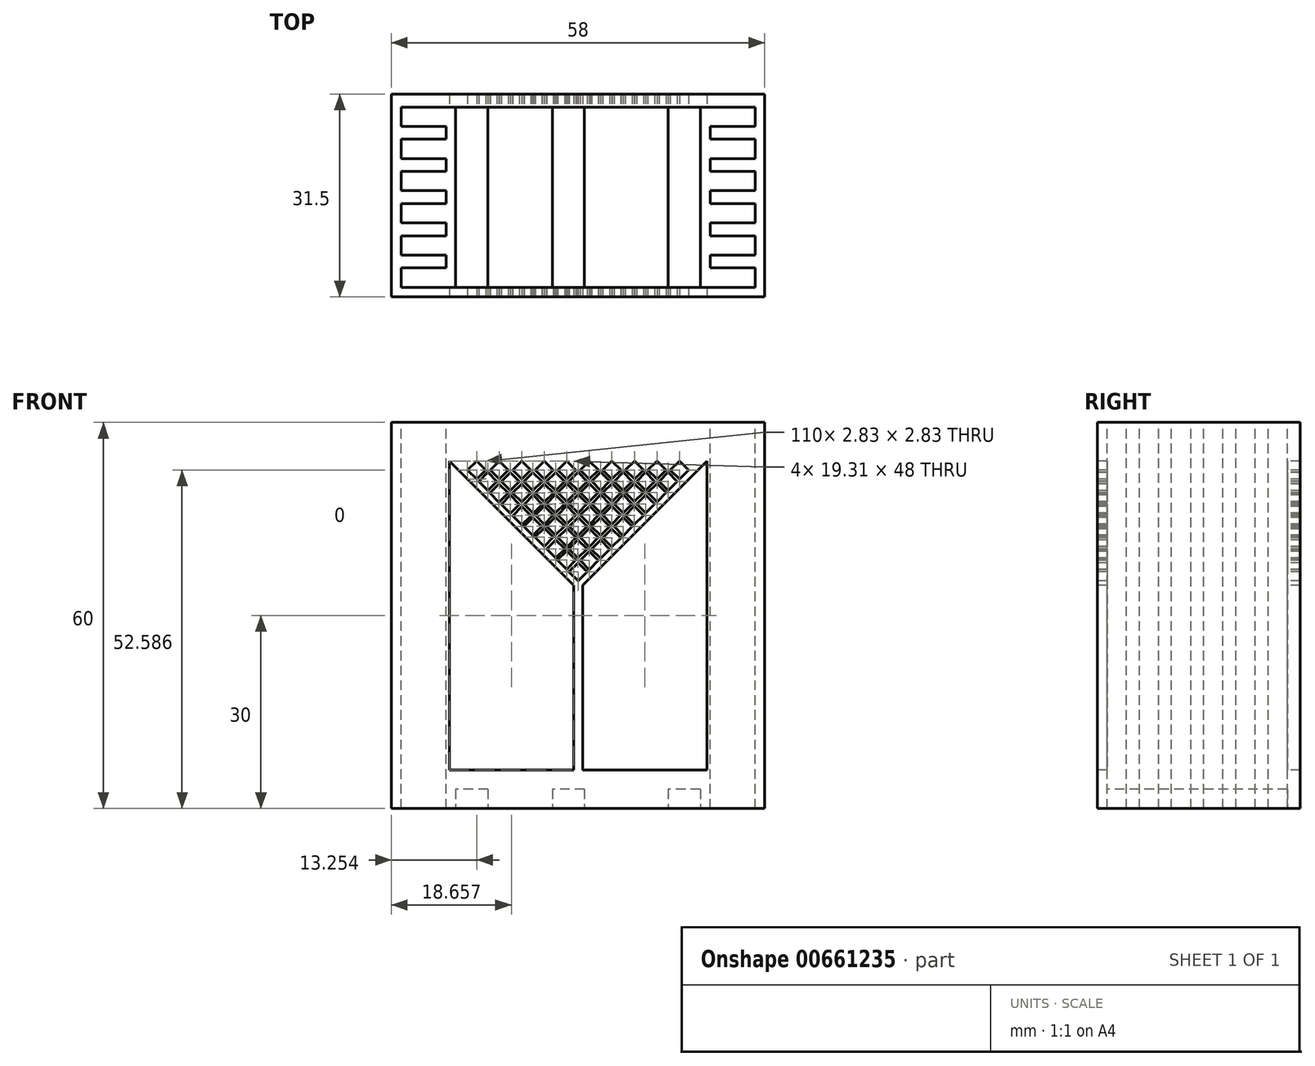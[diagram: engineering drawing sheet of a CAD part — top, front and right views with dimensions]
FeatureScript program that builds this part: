
annotation { "Feature Type Name" : "Feature", "Feature Type Description" : "" }
export const myFeature = defineFeature(function(context is Context, id is Id, definition is map)
    precondition{}
    {
        {
            var Q0;
            Q0=qCreatedBy(makeId("Top.planeOp"),FACE);
            var sketch = newSketch(context, id + "F0", { "sketchPlane" : qUnion([Q0])});
            skLineSegment(sketch, "E0.bottom", {"start": v(-21.86, 4.5) * mm, "end": v(36.14, 4.5) * mm});
            skLineSegment(sketch, "E0.left", {"start": v(-21.86, 4.5) * mm, "end": v(-21.86, -27) * mm});
            skLineSegment(sketch, "E0.right", {"start": v(36.14, 4.5) * mm, "end": v(36.14, -27) * mm});
            skLineSegment(sketch, "E1.bottom", {"start": v(-20.36, 3) * mm, "end": v(34.64, 3) * mm});
            skLineSegment(sketch, "E1.left", {"start": v(-20.36, 3) * mm, "end": v(-20.36, 0) * mm});
            skLineSegment(sketch, "E1.right", {"start": v(34.64, 3) * mm, "end": v(34.64, 0) * mm});
            skLineSegment(sketch, "E2", {"start": v(-20.36, 0) * mm, "end": v(-13.36, 0) * mm});
            skLineSegment(sketch, "E3", {"start": v(-13.36, 0) * mm, "end": v(-13.36, -2) * mm});
            skLineSegment(sketch, "E4", {"start": v(-13.36, -2) * mm, "end": v(-20.36, -2) * mm});
            skLineSegment(sketch, "E5", {"start": v(-20.36, -2) * mm, "end": v(-20.36, -5) * mm});
            skLineSegment(sketch, "E6.0.1.0", {"start": v(-20.36, -5) * mm, "end": v(-13.36, -5) * mm});
            skLineSegment(sketch, "E6.0.1.1", {"start": v(-13.36, -5) * mm, "end": v(-13.36, -7) * mm});
            skLineSegment(sketch, "E6.0.1.2", {"start": v(-20.36, -7) * mm, "end": v(-20.36, -10) * mm});
            skLineSegment(sketch, "E6.0.1.3", {"start": v(-13.36, -7) * mm, "end": v(-20.36, -7) * mm});
            skLineSegment(sketch, "E6.0.2.0", {"start": v(-20.36, -10) * mm, "end": v(-13.36, -10) * mm});
            skLineSegment(sketch, "E6.0.2.1", {"start": v(-13.36, -10) * mm, "end": v(-13.36, -12) * mm});
            skLineSegment(sketch, "E6.0.2.2", {"start": v(-20.36, -12) * mm, "end": v(-20.36, -15) * mm});
            skLineSegment(sketch, "E6.0.2.3", {"start": v(-13.36, -12) * mm, "end": v(-20.36, -12) * mm});
            skLineSegment(sketch, "E6.0.3.0", {"start": v(-20.36, -15) * mm, "end": v(-13.36, -15) * mm});
            skLineSegment(sketch, "E6.0.3.1", {"start": v(-13.36, -15) * mm, "end": v(-13.36, -17) * mm});
            skLineSegment(sketch, "E6.0.3.2", {"start": v(-20.36, -17) * mm, "end": v(-20.36, -20) * mm});
            skLineSegment(sketch, "E6.0.3.3", {"start": v(-13.36, -17) * mm, "end": v(-20.36, -17) * mm});
            skLineSegment(sketch, "E6.0.4.0", {"start": v(-20.36, -20) * mm, "end": v(-13.36, -20) * mm});
            skLineSegment(sketch, "E6.0.4.1", {"start": v(-13.36, -20) * mm, "end": v(-13.36, -22) * mm});
            skLineSegment(sketch, "E6.0.4.2", {"start": v(-20.36, -22) * mm, "end": v(-20.36, -25) * mm});
            skLineSegment(sketch, "E6.0.4.3", {"start": v(-13.36, -22) * mm, "end": v(-20.36, -22) * mm});
            skLineSegment(sketch, "E6.direction1", {"start": v(-20.36, -5) * mm, "end": v(4.64, -5) * mm, "construction": true});
            skLineSegment(sketch, "E6.direction2", {"start": v(-20.36, -5) * mm, "end": v(-20.36, -10) * mm, "construction": true});
            skLineSegment(sketch, "E7.0.1.2", {"start": v(34.64, -25) * mm, "end": v(34.64, -22) * mm});
            skLineSegment(sketch, "E7.0.2.0", {"start": v(34.64, -22) * mm, "end": v(27.64, -22) * mm});
            skLineSegment(sketch, "E7.0.2.1", {"start": v(27.64, -22) * mm, "end": v(27.64, -20) * mm});
            skLineSegment(sketch, "E7.0.2.2", {"start": v(34.64, -20) * mm, "end": v(34.64, -17) * mm});
            skLineSegment(sketch, "E7.0.2.3", {"start": v(27.64, -20) * mm, "end": v(34.64, -20) * mm});
            skLineSegment(sketch, "E7.0.3.0", {"start": v(34.64, -17) * mm, "end": v(27.64, -17) * mm});
            skLineSegment(sketch, "E7.0.3.1", {"start": v(27.64, -17) * mm, "end": v(27.64, -15) * mm});
            skLineSegment(sketch, "E7.0.3.2", {"start": v(34.64, -15) * mm, "end": v(34.64, -12) * mm});
            skLineSegment(sketch, "E7.0.3.3", {"start": v(27.64, -15) * mm, "end": v(34.64, -15) * mm});
            skLineSegment(sketch, "E7.0.4.0", {"start": v(34.64, -12) * mm, "end": v(27.64, -12) * mm});
            skLineSegment(sketch, "E7.0.4.1", {"start": v(27.64, -12) * mm, "end": v(27.64, -10) * mm});
            skLineSegment(sketch, "E7.0.4.2", {"start": v(34.64, -10) * mm, "end": v(34.64, -7) * mm});
            skLineSegment(sketch, "E7.0.4.3", {"start": v(27.64, -10) * mm, "end": v(34.64, -10) * mm});
            skLineSegment(sketch, "E7.0.5.0", {"start": v(34.64, -7) * mm, "end": v(27.64, -7) * mm});
            skLineSegment(sketch, "E7.0.5.1", {"start": v(27.64, -7) * mm, "end": v(27.64, -5) * mm});
            skLineSegment(sketch, "E7.0.5.2", {"start": v(34.64, -5) * mm, "end": v(34.64, -2) * mm});
            skLineSegment(sketch, "E7.0.5.3", {"start": v(27.64, -5) * mm, "end": v(34.64, -5) * mm});
            skLineSegment(sketch, "E7.0.6.0", {"start": v(34.64, -2) * mm, "end": v(27.64, -2) * mm});
            skLineSegment(sketch, "E7.0.6.1", {"start": v(27.64, -2) * mm, "end": v(27.64, 0) * mm});
            skLineSegment(sketch, "E7.0.6.2", {"start": v(34.64, 0) * mm, "end": v(34.64, 3) * mm});
            skLineSegment(sketch, "E7.0.6.3", {"start": v(27.64, 0) * mm, "end": v(34.64, 0) * mm});
            skLineSegment(sketch, "E7.direction2", {"start": v(34.64, -27) * mm, "end": v(34.64, -22) * mm, "construction": true});
            skLineSegment(sketch, "E8", {"start": v(36.14, -27) * mm, "end": v(-21.86, -27) * mm});
            skLineSegment(sketch, "E9", {"start": v(34.64, -25) * mm, "end": v(-20.36, -25) * mm});
            skSolve(sketch);
        }
        {
            var Q0;
            Q0=makeQuery(id+"F0.imprint","IMPRINT",FACE,{"disambiguationData":[TD([[makeQuery(id+"F0.imprint","IMPRINT",EDGE,{"derivedFrom":sQuery(id+"F0.wireOp",EDGE,"E0.bottom")}),-1.0]])]});
            extrude(context, id + "F1", {"entities" : qUnion([Q0]), "depth" : 60 * mm, "offsetDistance" : 25 * mm});
        }
        {
            var Q0;
            Q0=makeQuery(id+"F1.opExtrude","SWEPT_FACE",FACE,{"disambiguationData":[OSD([sQuery(id+"F0.wireOp",EDGE,"E0.bottom")])]});
            var sketch = newSketch(context, id + "F2", { "sketchPlane" : qUnion([Q0])});
            skLineSegment(sketch, "E10.bottom", {"start": v(-27.14, 6) * mm, "end": v(12.86, 6) * mm});
            skLineSegment(sketch, "E10.top", {"start": v(-27.14, 54) * mm, "end": v(12.86, 54) * mm});
            skLineSegment(sketch, "E10.left", {"start": v(-27.14, 6) * mm, "end": v(-27.14, 54) * mm});
            skLineSegment(sketch, "E10.right", {"start": v(12.86, 6) * mm, "end": v(12.86, 54) * mm});
            skLineSegment(sketch, "E11", {"start": v(12.86, 6) * mm, "end": v(-6.45, 25.3) * mm});
            skLineSegment(sketch, "E12", {"start": v(-6.45, 25.3) * mm, "end": v(-6.45, 54) * mm});
            skLineSegment(sketch, "E13", {"start": v(-6.45, 54) * mm, "end": v(-7.84, 54) * mm});
            skLineSegment(sketch, "E14", {"start": v(-7.84, 54) * mm, "end": v(-7.84, 25.3) * mm});
            skLineSegment(sketch, "E15", {"start": v(-7.84, 25.3) * mm, "end": v(-27.14, 6) * mm});
            skLineSegment(sketch, "E16", {"start": v(8.6, 6) * mm, "end": v(10.02, 7.41) * mm});
            skLineSegment(sketch, "E17", {"start": v(10.02, 7.41) * mm, "end": v(8.6, 8.83) * mm});
            skLineSegment(sketch, "E18", {"start": v(8.6, 8.83) * mm, "end": v(7.2, 7.41) * mm});
            skLineSegment(sketch, "E19", {"start": v(7.2, 7.41) * mm, "end": v(8.6, 6) * mm});
            skLineSegment(sketch, "E20.1.0.0", {"start": v(6.52, 7.41) * mm, "end": v(5.1, 8.83) * mm});
            skLineSegment(sketch, "E20.1.0.1", {"start": v(5.1, 8.83) * mm, "end": v(3.7, 7.41) * mm});
            skLineSegment(sketch, "E20.1.0.2", {"start": v(3.7, 7.41) * mm, "end": v(5.1, 6) * mm});
            skLineSegment(sketch, "E20.1.0.3", {"start": v(5.1, 6) * mm, "end": v(6.52, 7.41) * mm});
            skLineSegment(sketch, "E20.2.0.0", {"start": v(3.02, 7.41) * mm, "end": v(1.6, 8.83) * mm});
            skLineSegment(sketch, "E20.2.0.1", {"start": v(1.6, 8.83) * mm, "end": v(0.2, 7.41) * mm});
            skLineSegment(sketch, "E20.2.0.2", {"start": v(0.2, 7.41) * mm, "end": v(1.6, 6) * mm});
            skLineSegment(sketch, "E20.2.0.3", {"start": v(1.6, 6) * mm, "end": v(3.02, 7.41) * mm});
            skLineSegment(sketch, "E20.3.0.0", {"start": v(-0.48, 7.41) * mm, "end": v(-1.9, 8.83) * mm});
            skLineSegment(sketch, "E20.3.0.1", {"start": v(-1.9, 8.83) * mm, "end": v(-3.3, 7.41) * mm});
            skLineSegment(sketch, "E20.3.0.2", {"start": v(-3.3, 7.41) * mm, "end": v(-1.9, 6) * mm});
            skLineSegment(sketch, "E20.3.0.3", {"start": v(-1.9, 6) * mm, "end": v(-0.48, 7.41) * mm});
            skLineSegment(sketch, "E20.4.0.0", {"start": v(-3.98, 7.41) * mm, "end": v(-5.4, 8.83) * mm});
            skLineSegment(sketch, "E20.4.0.1", {"start": v(-5.4, 8.83) * mm, "end": v(-6.8, 7.41) * mm});
            skLineSegment(sketch, "E20.4.0.2", {"start": v(-6.8, 7.41) * mm, "end": v(-5.4, 6) * mm});
            skLineSegment(sketch, "E20.4.0.3", {"start": v(-5.4, 6) * mm, "end": v(-3.98, 7.41) * mm});
            skLineSegment(sketch, "E20.5.0.0", {"start": v(-7.48, 7.41) * mm, "end": v(-8.9, 8.83) * mm});
            skLineSegment(sketch, "E20.5.0.1", {"start": v(-8.9, 8.83) * mm, "end": v(-10.3, 7.41) * mm});
            skLineSegment(sketch, "E20.5.0.2", {"start": v(-10.3, 7.41) * mm, "end": v(-8.9, 6) * mm});
            skLineSegment(sketch, "E20.5.0.3", {"start": v(-8.9, 6) * mm, "end": v(-7.48, 7.41) * mm});
            skLineSegment(sketch, "E20.6.0.0", {"start": v(-10.98, 7.41) * mm, "end": v(-12.4, 8.83) * mm});
            skLineSegment(sketch, "E20.6.0.1", {"start": v(-12.4, 8.83) * mm, "end": v(-13.8, 7.41) * mm});
            skLineSegment(sketch, "E20.6.0.2", {"start": v(-13.8, 7.41) * mm, "end": v(-12.4, 6) * mm});
            skLineSegment(sketch, "E20.6.0.3", {"start": v(-12.4, 6) * mm, "end": v(-10.98, 7.41) * mm});
            skLineSegment(sketch, "E20.direction1", {"start": v(10.02, 7.41) * mm, "end": v(6.52, 7.41) * mm, "construction": true});
            skLineSegment(sketch, "E21.0.7.0", {"start": v(-14.48, 7.41) * mm, "end": v(-15.9, 8.83) * mm});
            skLineSegment(sketch, "E21.3.7.0", {"start": v(-15.9, 8.83) * mm, "end": v(-17.3, 7.41) * mm});
            skLineSegment(sketch, "E21.6.7.0", {"start": v(-17.3, 7.41) * mm, "end": v(-15.9, 6) * mm});
            skLineSegment(sketch, "E21.9.7.0", {"start": v(-15.9, 6) * mm, "end": v(-14.48, 7.41) * mm});
            skLineSegment(sketch, "E21.0.8.0", {"start": v(-17.98, 7.41) * mm, "end": v(-19.4, 8.83) * mm});
            skLineSegment(sketch, "E21.3.8.0", {"start": v(-19.4, 8.83) * mm, "end": v(-20.8, 7.41) * mm});
            skLineSegment(sketch, "E21.6.8.0", {"start": v(-20.8, 7.41) * mm, "end": v(-19.4, 6) * mm});
            skLineSegment(sketch, "E21.9.8.0", {"start": v(-19.4, 6) * mm, "end": v(-17.98, 7.41) * mm});
            skLineSegment(sketch, "E22.0.9.0", {"start": v(-21.48, 7.41) * mm, "end": v(-22.9, 8.83) * mm});
            skLineSegment(sketch, "E22.3.9.0", {"start": v(-22.9, 8.83) * mm, "end": v(-24.3, 7.41) * mm});
            skLineSegment(sketch, "E22.6.9.0", {"start": v(-24.3, 7.41) * mm, "end": v(-22.9, 6) * mm});
            skLineSegment(sketch, "E22.9.9.0", {"start": v(-22.9, 6) * mm, "end": v(-21.48, 7.41) * mm});
            skLineSegment(sketch, "E23.direction1", {"start": v(6.87, 7.77) * mm, "end": v(3.37, 7.77) * mm, "construction": true});
            skLineSegment(sketch, "E24.1.0.0", {"start": v(-19.73, 9.17) * mm, "end": v(-21.14, 10.58) * mm});
            skLineSegment(sketch, "E24.1.0.1", {"start": v(-21.14, 10.58) * mm, "end": v(-22.56, 9.17) * mm});
            skLineSegment(sketch, "E24.1.0.2", {"start": v(-21.14, 7.76) * mm, "end": v(-19.73, 9.17) * mm});
            skLineSegment(sketch, "E24.1.0.3", {"start": v(-22.56, 9.17) * mm, "end": v(-21.14, 7.76) * mm});
            skLineSegment(sketch, "E24.2.0.0", {"start": v(-17.98, 10.93) * mm, "end": v(-19.4, 12.34) * mm});
            skLineSegment(sketch, "E24.2.0.1", {"start": v(-19.4, 12.34) * mm, "end": v(-20.8, 10.93) * mm});
            skLineSegment(sketch, "E24.2.0.2", {"start": v(-19.4, 9.51) * mm, "end": v(-17.98, 10.93) * mm});
            skLineSegment(sketch, "E24.2.0.3", {"start": v(-20.8, 10.93) * mm, "end": v(-19.4, 9.51) * mm});
            skLineSegment(sketch, "E24.3.0.0", {"start": v(-16.23, 12.68) * mm, "end": v(-17.64, 14.1) * mm});
            skLineSegment(sketch, "E24.3.0.1", {"start": v(-17.64, 14.1) * mm, "end": v(-19.06, 12.68) * mm});
            skLineSegment(sketch, "E24.3.0.2", {"start": v(-17.64, 11.27) * mm, "end": v(-16.23, 12.68) * mm});
            skLineSegment(sketch, "E24.3.0.3", {"start": v(-19.06, 12.68) * mm, "end": v(-17.64, 11.27) * mm});
            skLineSegment(sketch, "E24.4.0.0", {"start": v(-14.48, 14.44) * mm, "end": v(-15.9, 15.85) * mm});
            skLineSegment(sketch, "E24.4.0.1", {"start": v(-15.9, 15.85) * mm, "end": v(-17.3, 14.44) * mm});
            skLineSegment(sketch, "E24.4.0.2", {"start": v(-15.9, 13.03) * mm, "end": v(-14.48, 14.44) * mm});
            skLineSegment(sketch, "E24.4.0.3", {"start": v(-17.3, 14.44) * mm, "end": v(-15.9, 13.03) * mm});
            skLineSegment(sketch, "E24.5.0.0", {"start": v(-12.73, 16.2) * mm, "end": v(-14.14, 17.61) * mm});
            skLineSegment(sketch, "E24.5.0.1", {"start": v(-14.14, 17.61) * mm, "end": v(-15.55, 16.2) * mm});
            skLineSegment(sketch, "E24.5.0.2", {"start": v(-14.14, 14.78) * mm, "end": v(-12.73, 16.2) * mm});
            skLineSegment(sketch, "E24.5.0.3", {"start": v(-15.55, 16.2) * mm, "end": v(-14.14, 14.78) * mm});
            skLineSegment(sketch, "E24.6.0.0", {"start": v(-10.97, 17.95) * mm, "end": v(-12.39, 19.37) * mm});
            skLineSegment(sketch, "E24.6.0.1", {"start": v(-12.39, 19.37) * mm, "end": v(-13.8, 17.95) * mm});
            skLineSegment(sketch, "E24.6.0.2", {"start": v(-12.39, 16.54) * mm, "end": v(-10.97, 17.95) * mm});
            skLineSegment(sketch, "E24.6.0.3", {"start": v(-13.8, 17.95) * mm, "end": v(-12.39, 16.54) * mm});
            skLineSegment(sketch, "E24.7.0.0", {"start": v(-9.22, 19.7) * mm, "end": v(-10.64, 21.12) * mm});
            skLineSegment(sketch, "E24.7.0.1", {"start": v(-10.64, 21.12) * mm, "end": v(-12.05, 19.7) * mm});
            skLineSegment(sketch, "E24.7.0.2", {"start": v(-10.64, 18.3) * mm, "end": v(-9.22, 19.7) * mm});
            skLineSegment(sketch, "E24.7.0.3", {"start": v(-12.05, 19.7) * mm, "end": v(-10.64, 18.3) * mm});
            skLineSegment(sketch, "E24.8.0.0", {"start": v(-7.47, 21.47) * mm, "end": v(-8.89, 22.88) * mm});
            skLineSegment(sketch, "E24.8.0.1", {"start": v(-8.89, 22.88) * mm, "end": v(-10.3, 21.47) * mm});
            skLineSegment(sketch, "E24.8.0.2", {"start": v(-8.89, 20.05) * mm, "end": v(-7.47, 21.47) * mm});
            skLineSegment(sketch, "E24.8.0.3", {"start": v(-10.3, 21.47) * mm, "end": v(-8.89, 20.05) * mm});
            skLineSegment(sketch, "E24.9.0.0", {"start": v(-5.72, 23.22) * mm, "end": v(-7.14, 24.64) * mm});
            skLineSegment(sketch, "E24.9.0.1", {"start": v(-7.14, 24.64) * mm, "end": v(-8.55, 23.22) * mm});
            skLineSegment(sketch, "E24.9.0.2", {"start": v(-7.14, 21.8) * mm, "end": v(-5.72, 23.22) * mm});
            skLineSegment(sketch, "E24.9.0.3", {"start": v(-8.55, 23.22) * mm, "end": v(-7.14, 21.8) * mm});
            skLineSegment(sketch, "E24.direction1", {"start": v(-22.9, 6) * mm, "end": v(-21.14, 7.76) * mm, "construction": true});
            skLineSegment(sketch, "E25.1.0.0", {"start": v(-17.64, 7.75) * mm, "end": v(-16.23, 9.16) * mm});
            skLineSegment(sketch, "E25.1.0.1", {"start": v(-19.05, 9.16) * mm, "end": v(-17.64, 7.75) * mm});
            skLineSegment(sketch, "E25.1.0.2", {"start": v(-17.64, 10.58) * mm, "end": v(-19.05, 9.16) * mm});
            skLineSegment(sketch, "E25.1.0.3", {"start": v(-16.23, 9.16) * mm, "end": v(-17.64, 10.58) * mm});
            skLineSegment(sketch, "E25.2.0.0", {"start": v(-15.89, 9.5) * mm, "end": v(-14.47, 10.91) * mm});
            skLineSegment(sketch, "E25.2.0.1", {"start": v(-17.3, 10.91) * mm, "end": v(-15.89, 9.5) * mm});
            skLineSegment(sketch, "E25.2.0.2", {"start": v(-15.89, 12.33) * mm, "end": v(-17.3, 10.91) * mm});
            skLineSegment(sketch, "E25.2.0.3", {"start": v(-14.47, 10.91) * mm, "end": v(-15.89, 12.33) * mm});
            skLineSegment(sketch, "E25.3.0.0", {"start": v(-14.13, 11.25) * mm, "end": v(-12.72, 12.66) * mm});
            skLineSegment(sketch, "E25.3.0.1", {"start": v(-15.55, 12.66) * mm, "end": v(-14.13, 11.25) * mm});
            skLineSegment(sketch, "E25.3.0.2", {"start": v(-14.13, 14.08) * mm, "end": v(-15.55, 12.66) * mm});
            skLineSegment(sketch, "E25.3.0.3", {"start": v(-12.72, 12.66) * mm, "end": v(-14.13, 14.08) * mm});
            skLineSegment(sketch, "E25.4.0.0", {"start": v(-12.38, 13) * mm, "end": v(-10.96, 14.41) * mm});
            skLineSegment(sketch, "E25.4.0.1", {"start": v(-13.8, 14.41) * mm, "end": v(-12.38, 13) * mm});
            skLineSegment(sketch, "E25.4.0.2", {"start": v(-12.38, 15.83) * mm, "end": v(-13.8, 14.41) * mm});
            skLineSegment(sketch, "E25.4.0.3", {"start": v(-10.96, 14.41) * mm, "end": v(-12.38, 15.83) * mm});
            skLineSegment(sketch, "E25.5.0.0", {"start": v(-10.63, 14.75) * mm, "end": v(-9.21, 16.16) * mm});
            skLineSegment(sketch, "E25.5.0.1", {"start": v(-12.04, 16.16) * mm, "end": v(-10.63, 14.75) * mm});
            skLineSegment(sketch, "E25.5.0.2", {"start": v(-10.63, 17.58) * mm, "end": v(-12.04, 16.16) * mm});
            skLineSegment(sketch, "E25.5.0.3", {"start": v(-9.21, 16.16) * mm, "end": v(-10.63, 17.58) * mm});
            skLineSegment(sketch, "E25.6.0.0", {"start": v(-8.87, 16.5) * mm, "end": v(-7.46, 17.91) * mm});
            skLineSegment(sketch, "E25.6.0.1", {"start": v(-10.29, 17.91) * mm, "end": v(-8.87, 16.5) * mm});
            skLineSegment(sketch, "E25.6.0.2", {"start": v(-8.87, 19.33) * mm, "end": v(-10.29, 17.91) * mm});
            skLineSegment(sketch, "E25.6.0.3", {"start": v(-7.46, 17.91) * mm, "end": v(-8.87, 19.33) * mm});
            skLineSegment(sketch, "E25.7.0.0", {"start": v(-7.12, 18.25) * mm, "end": v(-5.7, 19.66) * mm});
            skLineSegment(sketch, "E25.7.0.1", {"start": v(-8.53, 19.66) * mm, "end": v(-7.12, 18.25) * mm});
            skLineSegment(sketch, "E25.7.0.2", {"start": v(-7.12, 21.08) * mm, "end": v(-8.53, 19.66) * mm});
            skLineSegment(sketch, "E25.7.0.3", {"start": v(-5.7, 19.66) * mm, "end": v(-7.12, 21.08) * mm});
            skLineSegment(sketch, "E25.8.0.0", {"start": v(-5.36, 20) * mm, "end": v(-3.95, 21.41) * mm});
            skLineSegment(sketch, "E25.8.0.1", {"start": v(-6.78, 21.41) * mm, "end": v(-5.36, 20) * mm});
            skLineSegment(sketch, "E25.8.0.2", {"start": v(-5.36, 22.83) * mm, "end": v(-6.78, 21.41) * mm});
            skLineSegment(sketch, "E25.8.0.3", {"start": v(-3.95, 21.41) * mm, "end": v(-5.36, 22.83) * mm});
            skLineSegment(sketch, "E25.direction1", {"start": v(-19.4, 6) * mm, "end": v(-17.64, 7.75) * mm, "construction": true});
            skLineSegment(sketch, "E26.1.0.0", {"start": v(-14.15, 7.75) * mm, "end": v(-12.74, 9.16) * mm});
            skLineSegment(sketch, "E26.1.0.1", {"start": v(-15.56, 9.16) * mm, "end": v(-14.15, 7.75) * mm});
            skLineSegment(sketch, "E26.1.0.2", {"start": v(-14.15, 10.58) * mm, "end": v(-15.56, 9.16) * mm});
            skLineSegment(sketch, "E26.1.0.3", {"start": v(-12.74, 9.16) * mm, "end": v(-14.15, 10.58) * mm});
            skLineSegment(sketch, "E26.2.0.0", {"start": v(-12.4, 9.5) * mm, "end": v(-11, 10.91) * mm});
            skLineSegment(sketch, "E26.2.0.1", {"start": v(-13.82, 10.91) * mm, "end": v(-12.4, 9.5) * mm});
            skLineSegment(sketch, "E26.2.0.2", {"start": v(-12.4, 12.33) * mm, "end": v(-13.82, 10.91) * mm});
            skLineSegment(sketch, "E26.2.0.3", {"start": v(-11, 10.91) * mm, "end": v(-12.4, 12.33) * mm});
            skLineSegment(sketch, "E26.3.0.0", {"start": v(-10.66, 11.25) * mm, "end": v(-9.25, 12.66) * mm});
            skLineSegment(sketch, "E26.3.0.1", {"start": v(-12.08, 12.66) * mm, "end": v(-10.66, 11.25) * mm});
            skLineSegment(sketch, "E26.3.0.2", {"start": v(-10.66, 14.08) * mm, "end": v(-12.08, 12.66) * mm});
            skLineSegment(sketch, "E26.3.0.3", {"start": v(-9.25, 12.66) * mm, "end": v(-10.66, 14.08) * mm});
            skLineSegment(sketch, "E26.4.0.0", {"start": v(-8.92, 13) * mm, "end": v(-7.5, 14.41) * mm});
            skLineSegment(sketch, "E26.4.0.1", {"start": v(-10.33, 14.41) * mm, "end": v(-8.92, 13) * mm});
            skLineSegment(sketch, "E26.4.0.2", {"start": v(-8.92, 15.83) * mm, "end": v(-10.33, 14.41) * mm});
            skLineSegment(sketch, "E26.4.0.3", {"start": v(-7.5, 14.41) * mm, "end": v(-8.92, 15.83) * mm});
            skLineSegment(sketch, "E26.5.0.0", {"start": v(-7.18, 14.75) * mm, "end": v(-5.76, 16.16) * mm});
            skLineSegment(sketch, "E26.5.0.1", {"start": v(-8.59, 16.16) * mm, "end": v(-7.18, 14.75) * mm});
            skLineSegment(sketch, "E26.5.0.2", {"start": v(-7.18, 17.58) * mm, "end": v(-8.59, 16.16) * mm});
            skLineSegment(sketch, "E26.5.0.3", {"start": v(-5.76, 16.16) * mm, "end": v(-7.18, 17.58) * mm});
            skLineSegment(sketch, "E26.6.0.0", {"start": v(-5.43, 16.5) * mm, "end": v(-4.02, 17.91) * mm});
            skLineSegment(sketch, "E26.6.0.1", {"start": v(-6.85, 17.91) * mm, "end": v(-5.43, 16.5) * mm});
            skLineSegment(sketch, "E26.6.0.2", {"start": v(-5.43, 19.33) * mm, "end": v(-6.85, 17.91) * mm});
            skLineSegment(sketch, "E26.6.0.3", {"start": v(-4.02, 17.91) * mm, "end": v(-5.43, 19.33) * mm});
            skLineSegment(sketch, "E26.7.0.0", {"start": v(-3.69, 18.25) * mm, "end": v(-2.27, 19.66) * mm});
            skLineSegment(sketch, "E26.7.0.1", {"start": v(-5.1, 19.66) * mm, "end": v(-3.69, 18.25) * mm});
            skLineSegment(sketch, "E26.7.0.2", {"start": v(-3.69, 21.08) * mm, "end": v(-5.1, 19.66) * mm});
            skLineSegment(sketch, "E26.7.0.3", {"start": v(-2.27, 19.66) * mm, "end": v(-3.69, 21.08) * mm});
            skLineSegment(sketch, "E26.direction1", {"start": v(-15.9, 6) * mm, "end": v(-14.15, 7.75) * mm, "construction": true});
            skLineSegment(sketch, "E27.1.0.0", {"start": v(-10.64, 7.74) * mm, "end": v(-9.23, 9.15) * mm});
            skLineSegment(sketch, "E27.1.0.1", {"start": v(-9.23, 9.15) * mm, "end": v(-10.64, 10.57) * mm});
            skLineSegment(sketch, "E27.1.0.2", {"start": v(-10.64, 10.57) * mm, "end": v(-12.05, 9.15) * mm});
            skLineSegment(sketch, "E27.1.0.3", {"start": v(-12.05, 9.15) * mm, "end": v(-10.64, 7.74) * mm});
            skLineSegment(sketch, "E27.2.0.0", {"start": v(-8.89, 9.48) * mm, "end": v(-7.47, 10.9) * mm});
            skLineSegment(sketch, "E27.2.0.1", {"start": v(-7.47, 10.9) * mm, "end": v(-8.89, 12.3) * mm});
            skLineSegment(sketch, "E27.2.0.2", {"start": v(-8.89, 12.3) * mm, "end": v(-10.3, 10.9) * mm});
            skLineSegment(sketch, "E27.2.0.3", {"start": v(-10.3, 10.9) * mm, "end": v(-8.89, 9.48) * mm});
            skLineSegment(sketch, "E27.3.0.0", {"start": v(-7.13, 11.22) * mm, "end": v(-5.72, 12.63) * mm});
            skLineSegment(sketch, "E27.3.0.1", {"start": v(-5.72, 12.63) * mm, "end": v(-7.13, 14.05) * mm});
            skLineSegment(sketch, "E27.3.0.2", {"start": v(-7.13, 14.05) * mm, "end": v(-8.55, 12.63) * mm});
            skLineSegment(sketch, "E27.3.0.3", {"start": v(-8.55, 12.63) * mm, "end": v(-7.13, 11.22) * mm});
            skLineSegment(sketch, "E27.4.0.0", {"start": v(-5.38, 12.96) * mm, "end": v(-3.96, 14.37) * mm});
            skLineSegment(sketch, "E27.4.0.1", {"start": v(-3.96, 14.37) * mm, "end": v(-5.38, 15.79) * mm});
            skLineSegment(sketch, "E27.4.0.2", {"start": v(-5.38, 15.79) * mm, "end": v(-6.8, 14.37) * mm});
            skLineSegment(sketch, "E27.4.0.3", {"start": v(-6.8, 14.37) * mm, "end": v(-5.38, 12.96) * mm});
            skLineSegment(sketch, "E27.5.0.0", {"start": v(-3.63, 14.7) * mm, "end": v(-2.21, 16.11) * mm});
            skLineSegment(sketch, "E27.5.0.1", {"start": v(-2.21, 16.11) * mm, "end": v(-3.63, 17.53) * mm});
            skLineSegment(sketch, "E27.5.0.2", {"start": v(-3.63, 17.53) * mm, "end": v(-5.04, 16.11) * mm});
            skLineSegment(sketch, "E27.5.0.3", {"start": v(-5.04, 16.11) * mm, "end": v(-3.63, 14.7) * mm});
            skLineSegment(sketch, "E27.6.0.0", {"start": v(-1.87, 16.44) * mm, "end": v(-0.46, 17.85) * mm});
            skLineSegment(sketch, "E27.6.0.1", {"start": v(-0.46, 17.85) * mm, "end": v(-1.87, 19.27) * mm});
            skLineSegment(sketch, "E27.6.0.2", {"start": v(-1.87, 19.27) * mm, "end": v(-3.29, 17.85) * mm});
            skLineSegment(sketch, "E27.6.0.3", {"start": v(-3.29, 17.85) * mm, "end": v(-1.87, 16.44) * mm});
            skLineSegment(sketch, "E27.direction1", {"start": v(-12.4, 6) * mm, "end": v(-10.64, 7.74) * mm, "construction": true});
            skLineSegment(sketch, "E28.1.0.0", {"start": v(-5.73, 9.16) * mm, "end": v(-7.14, 10.58) * mm});
            skLineSegment(sketch, "E28.1.0.1", {"start": v(-7.14, 7.75) * mm, "end": v(-5.73, 9.16) * mm});
            skLineSegment(sketch, "E28.1.0.2", {"start": v(-8.55, 9.16) * mm, "end": v(-7.14, 7.75) * mm});
            skLineSegment(sketch, "E28.1.0.3", {"start": v(-7.14, 10.58) * mm, "end": v(-8.55, 9.16) * mm});
            skLineSegment(sketch, "E28.2.0.0", {"start": v(-3.97, 10.91) * mm, "end": v(-5.39, 12.33) * mm});
            skLineSegment(sketch, "E28.2.0.1", {"start": v(-5.39, 9.5) * mm, "end": v(-3.97, 10.91) * mm});
            skLineSegment(sketch, "E28.2.0.2", {"start": v(-6.8, 10.91) * mm, "end": v(-5.39, 9.5) * mm});
            skLineSegment(sketch, "E28.2.0.3", {"start": v(-5.39, 12.33) * mm, "end": v(-6.8, 10.91) * mm});
            skLineSegment(sketch, "E28.3.0.0", {"start": v(-2.22, 12.66) * mm, "end": v(-3.63, 14.08) * mm});
            skLineSegment(sketch, "E28.3.0.1", {"start": v(-3.63, 11.25) * mm, "end": v(-2.22, 12.66) * mm});
            skLineSegment(sketch, "E28.3.0.2", {"start": v(-5.05, 12.66) * mm, "end": v(-3.63, 11.25) * mm});
            skLineSegment(sketch, "E28.3.0.3", {"start": v(-3.63, 14.08) * mm, "end": v(-5.05, 12.66) * mm});
            skLineSegment(sketch, "E28.4.0.0", {"start": v(-0.46, 14.41) * mm, "end": v(-1.88, 15.83) * mm});
            skLineSegment(sketch, "E28.4.0.1", {"start": v(-1.88, 13) * mm, "end": v(-0.46, 14.41) * mm});
            skLineSegment(sketch, "E28.4.0.2", {"start": v(-3.3, 14.41) * mm, "end": v(-1.88, 13) * mm});
            skLineSegment(sketch, "E28.4.0.3", {"start": v(-1.88, 15.83) * mm, "end": v(-3.3, 14.41) * mm});
            skLineSegment(sketch, "E28.5.0.0", {"start": v(1.29, 16.16) * mm, "end": v(-0.13, 17.58) * mm});
            skLineSegment(sketch, "E28.5.0.1", {"start": v(-0.13, 14.75) * mm, "end": v(1.29, 16.16) * mm});
            skLineSegment(sketch, "E28.5.0.2", {"start": v(-1.54, 16.16) * mm, "end": v(-0.13, 14.75) * mm});
            skLineSegment(sketch, "E28.5.0.3", {"start": v(-0.13, 17.58) * mm, "end": v(-1.54, 16.16) * mm});
            skLineSegment(sketch, "E28.direction1", {"start": v(-8.9, 6) * mm, "end": v(-7.14, 7.75) * mm, "construction": true});
            skLineSegment(sketch, "E29.1.0.0", {"start": v(-2.24, 9.18) * mm, "end": v(-3.65, 10.6) * mm});
            skLineSegment(sketch, "E29.1.0.1", {"start": v(-3.65, 7.77) * mm, "end": v(-2.24, 9.18) * mm});
            skLineSegment(sketch, "E29.1.0.2", {"start": v(-5.06, 9.18) * mm, "end": v(-3.65, 7.77) * mm});
            skLineSegment(sketch, "E29.1.0.3", {"start": v(-3.65, 10.6) * mm, "end": v(-5.06, 9.18) * mm});
            skLineSegment(sketch, "E29.2.0.0", {"start": v(-0.5, 10.95) * mm, "end": v(-1.9, 12.37) * mm});
            skLineSegment(sketch, "E29.2.0.1", {"start": v(-1.9, 9.54) * mm, "end": v(-0.5, 10.95) * mm});
            skLineSegment(sketch, "E29.2.0.2", {"start": v(-3.32, 10.95) * mm, "end": v(-1.9, 9.54) * mm});
            skLineSegment(sketch, "E29.2.0.3", {"start": v(-1.9, 12.37) * mm, "end": v(-3.32, 10.95) * mm});
            skLineSegment(sketch, "E29.3.0.0", {"start": v(1.25, 12.72) * mm, "end": v(-0.16, 14.14) * mm});
            skLineSegment(sketch, "E29.3.0.1", {"start": v(-0.16, 11.31) * mm, "end": v(1.25, 12.72) * mm});
            skLineSegment(sketch, "E29.3.0.2", {"start": v(-1.58, 12.72) * mm, "end": v(-0.16, 11.31) * mm});
            skLineSegment(sketch, "E29.3.0.3", {"start": v(-0.16, 14.14) * mm, "end": v(-1.58, 12.72) * mm});
            skLineSegment(sketch, "E29.4.0.0", {"start": v(3, 14.5) * mm, "end": v(1.58, 15.9) * mm});
            skLineSegment(sketch, "E29.4.0.1", {"start": v(1.58, 13.08) * mm, "end": v(3, 14.5) * mm});
            skLineSegment(sketch, "E29.4.0.2", {"start": v(0.17, 14.5) * mm, "end": v(1.58, 13.08) * mm});
            skLineSegment(sketch, "E29.4.0.3", {"start": v(1.58, 15.9) * mm, "end": v(0.17, 14.5) * mm});
            skLineSegment(sketch, "E29.direction1", {"start": v(-5.4, 6) * mm, "end": v(-3.65, 7.77) * mm, "construction": true});
            skLineSegment(sketch, "E30.1.0.0", {"start": v(-0.14, 10.6) * mm, "end": v(-1.55, 9.18) * mm});
            skLineSegment(sketch, "E30.1.0.1", {"start": v(-0.14, 7.77) * mm, "end": v(1.27, 9.18) * mm});
            skLineSegment(sketch, "E30.1.0.2", {"start": v(-1.55, 9.18) * mm, "end": v(-0.14, 7.77) * mm});
            skLineSegment(sketch, "E30.1.0.3", {"start": v(1.27, 9.18) * mm, "end": v(-0.14, 10.6) * mm});
            skLineSegment(sketch, "E30.2.0.0", {"start": v(1.61, 12.37) * mm, "end": v(0.2, 10.95) * mm});
            skLineSegment(sketch, "E30.2.0.1", {"start": v(1.61, 9.54) * mm, "end": v(3.03, 10.95) * mm});
            skLineSegment(sketch, "E30.2.0.2", {"start": v(0.2, 10.95) * mm, "end": v(1.61, 9.54) * mm});
            skLineSegment(sketch, "E30.2.0.3", {"start": v(3.03, 10.95) * mm, "end": v(1.61, 12.37) * mm});
            skLineSegment(sketch, "E30.3.0.0", {"start": v(3.37, 14.14) * mm, "end": v(1.95, 12.72) * mm});
            skLineSegment(sketch, "E30.3.0.1", {"start": v(3.37, 11.31) * mm, "end": v(4.78, 12.72) * mm});
            skLineSegment(sketch, "E30.3.0.2", {"start": v(1.95, 12.72) * mm, "end": v(3.37, 11.31) * mm});
            skLineSegment(sketch, "E30.3.0.3", {"start": v(4.78, 12.72) * mm, "end": v(3.37, 14.14) * mm});
            skLineSegment(sketch, "E30.direction1", {"start": v(-1.9, 6) * mm, "end": v(-0.14, 7.77) * mm, "construction": true});
            skLineSegment(sketch, "E31.1.0.0", {"start": v(3.37, 7.8) * mm, "end": v(4.78, 9.2) * mm});
            skLineSegment(sketch, "E31.1.0.1", {"start": v(4.78, 9.2) * mm, "end": v(3.37, 10.62) * mm});
            skLineSegment(sketch, "E31.1.0.2", {"start": v(3.37, 10.62) * mm, "end": v(1.96, 9.2) * mm});
            skLineSegment(sketch, "E31.1.0.3", {"start": v(1.96, 9.2) * mm, "end": v(3.37, 7.79) * mm});
            skLineSegment(sketch, "E31.2.0.0", {"start": v(5.13, 9.58) * mm, "end": v(6.55, 11) * mm});
            skLineSegment(sketch, "E31.2.0.1", {"start": v(6.55, 11) * mm, "end": v(5.13, 12.4) * mm});
            skLineSegment(sketch, "E31.2.0.2", {"start": v(5.13, 12.4) * mm, "end": v(3.72, 11) * mm});
            skLineSegment(sketch, "E31.2.0.3", {"start": v(3.72, 11) * mm, "end": v(5.13, 9.58) * mm});
            skLineSegment(sketch, "E31.direction1", {"start": v(1.6, 6) * mm, "end": v(3.37, 7.8) * mm, "construction": true});
            skLineSegment(sketch, "E32.1.0.0", {"start": v(6.86, 7.76) * mm, "end": v(8.27, 9.17) * mm});
            skLineSegment(sketch, "E32.1.0.1", {"start": v(5.45, 9.17) * mm, "end": v(6.86, 7.76) * mm});
            skLineSegment(sketch, "E32.1.0.2", {"start": v(6.86, 10.59) * mm, "end": v(5.45, 9.17) * mm});
            skLineSegment(sketch, "E32.1.0.3", {"start": v(8.27, 9.17) * mm, "end": v(6.86, 10.59) * mm});
            skLineSegment(sketch, "E32.direction1", {"start": v(5.1, 6) * mm, "end": v(6.86, 7.76) * mm, "construction": true});
            skSolve(sketch);
        }
        {
            var Q0;
            {var subQ0=sQuery(id+"F2.wireOp",EDGE,"E10.right");Q0=makeQuery(id+"F2.imprint","IMPRINT",FACE,{"disambiguationData":[TD([[makeQuery(id+"F2.imprint","IMPRINT",EDGE,{"derivedFrom":subQ0}),1.0]])]});}
            var Q1;
            {var subQ0=sQuery(id+"F2.wireOp",EDGE,"E10.left");Q1=makeQuery(id+"F2.imprint","IMPRINT",FACE,{"disambiguationData":[TD([[makeQuery(id+"F2.imprint","IMPRINT",EDGE,{"derivedFrom":subQ0}),-1.0]])]});}
            var Q2;
            Q2=makeQuery(id+"F2.imprint","IMPRINT",FACE,{"disambiguationData":[TD([[makeQuery(id+"F2.imprint","IMPRINT",EDGE,{"derivedFrom":sQuery(id+"F2.wireOp",EDGE,"E24.9.0.0")}),1.0]])]});
            var Q3;
            Q3=makeQuery(id+"F2.imprint","IMPRINT",FACE,{"disambiguationData":[TD([[makeQuery(id+"F2.imprint","IMPRINT",EDGE,{"derivedFrom":sQuery(id+"F2.wireOp",EDGE,"E24.8.0.0")}),1.0]])]});
            var Q4;
            Q4=makeQuery(id+"F2.imprint","IMPRINT",FACE,{"disambiguationData":[TD([[makeQuery(id+"F2.imprint","IMPRINT",EDGE,{"derivedFrom":sQuery(id+"F2.wireOp",EDGE,"E24.7.0.0")}),1.0]])]});
            var Q5;
            Q5=makeQuery(id+"F2.imprint","IMPRINT",FACE,{"disambiguationData":[TD([[makeQuery(id+"F2.imprint","IMPRINT",EDGE,{"derivedFrom":sQuery(id+"F2.wireOp",EDGE,"E24.6.0.0")}),1.0]])]});
            var Q6;
            Q6=makeQuery(id+"F2.imprint","IMPRINT",FACE,{"disambiguationData":[TD([[makeQuery(id+"F2.imprint","IMPRINT",EDGE,{"derivedFrom":sQuery(id+"F2.wireOp",EDGE,"E24.5.0.0")}),1.0]])]});
            var Q7;
            Q7=makeQuery(id+"F2.imprint","IMPRINT",FACE,{"disambiguationData":[TD([[makeQuery(id+"F2.imprint","IMPRINT",EDGE,{"derivedFrom":sQuery(id+"F2.wireOp",EDGE,"E24.4.0.0")}),1.0]])]});
            var Q8;
            Q8=makeQuery(id+"F2.imprint","IMPRINT",FACE,{"disambiguationData":[TD([[makeQuery(id+"F2.imprint","IMPRINT",EDGE,{"derivedFrom":sQuery(id+"F2.wireOp",EDGE,"E24.3.0.0")}),1.0]])]});
            var Q9;
            Q9=makeQuery(id+"F2.imprint","IMPRINT",FACE,{"disambiguationData":[TD([[makeQuery(id+"F2.imprint","IMPRINT",EDGE,{"derivedFrom":sQuery(id+"F2.wireOp",EDGE,"E24.2.0.0")}),1.0]])]});
            var Q10;
            Q10=makeQuery(id+"F2.imprint","IMPRINT",FACE,{"disambiguationData":[TD([[makeQuery(id+"F2.imprint","IMPRINT",EDGE,{"derivedFrom":sQuery(id+"F2.wireOp",EDGE,"E24.1.0.0")}),1.0]])]});
            var Q11;
            Q11=makeQuery(id+"F2.imprint","IMPRINT",FACE,{"disambiguationData":[TD([[makeQuery(id+"F2.imprint","IMPRINT",EDGE,{"derivedFrom":sQuery(id+"F2.wireOp",EDGE,"E22.0.9.0")}),1.0]])]});
            var Q12;
            Q12=makeQuery(id+"F2.imprint","IMPRINT",FACE,{"disambiguationData":[TD([[makeQuery(id+"F2.imprint","IMPRINT",EDGE,{"derivedFrom":sQuery(id+"F2.wireOp",EDGE,"E25.1.0.0")}),1.0]])]});
            var Q13;
            Q13=makeQuery(id+"F2.imprint","IMPRINT",FACE,{"disambiguationData":[TD([[makeQuery(id+"F2.imprint","IMPRINT",EDGE,{"derivedFrom":sQuery(id+"F2.wireOp",EDGE,"E21.0.7.0")}),1.0]])]});
            var Q14;
            Q14=makeQuery(id+"F2.imprint","IMPRINT",FACE,{"disambiguationData":[TD([[makeQuery(id+"F2.imprint","IMPRINT",EDGE,{"derivedFrom":sQuery(id+"F2.wireOp",EDGE,"E21.0.8.0")}),1.0]])]});
            var Q15;
            Q15=makeQuery(id+"F2.imprint","IMPRINT",FACE,{"disambiguationData":[TD([[makeQuery(id+"F2.imprint","IMPRINT",EDGE,{"derivedFrom":sQuery(id+"F2.wireOp",EDGE,"E25.2.0.0")}),1.0]])]});
            var Q16;
            Q16=makeQuery(id+"F2.imprint","IMPRINT",FACE,{"disambiguationData":[TD([[makeQuery(id+"F2.imprint","IMPRINT",EDGE,{"derivedFrom":sQuery(id+"F2.wireOp",EDGE,"E25.3.0.0")}),1.0]])]});
            var Q17;
            Q17=makeQuery(id+"F2.imprint","IMPRINT",FACE,{"disambiguationData":[TD([[makeQuery(id+"F2.imprint","IMPRINT",EDGE,{"derivedFrom":sQuery(id+"F2.wireOp",EDGE,"E25.4.0.0")}),1.0]])]});
            var Q18;
            Q18=makeQuery(id+"F2.imprint","IMPRINT",FACE,{"disambiguationData":[TD([[makeQuery(id+"F2.imprint","IMPRINT",EDGE,{"derivedFrom":sQuery(id+"F2.wireOp",EDGE,"E25.5.0.0")}),1.0]])]});
            var Q19;
            Q19=makeQuery(id+"F2.imprint","IMPRINT",FACE,{"disambiguationData":[TD([[makeQuery(id+"F2.imprint","IMPRINT",EDGE,{"derivedFrom":sQuery(id+"F2.wireOp",EDGE,"E25.6.0.0")}),1.0]])]});
            var Q20;
            Q20=makeQuery(id+"F2.imprint","IMPRINT",FACE,{"disambiguationData":[TD([[makeQuery(id+"F2.imprint","IMPRINT",EDGE,{"derivedFrom":sQuery(id+"F2.wireOp",EDGE,"E25.7.0.0")}),1.0]])]});
            var Q21;
            Q21=makeQuery(id+"F2.imprint","IMPRINT",FACE,{"disambiguationData":[TD([[makeQuery(id+"F2.imprint","IMPRINT",EDGE,{"derivedFrom":sQuery(id+"F2.wireOp",EDGE,"E25.8.0.0")}),1.0]])]});
            var Q22;
            Q22=makeQuery(id+"F2.imprint","IMPRINT",FACE,{"disambiguationData":[TD([[makeQuery(id+"F2.imprint","IMPRINT",EDGE,{"derivedFrom":sQuery(id+"F2.wireOp",EDGE,"E26.7.0.0")}),1.0]])]});
            var Q23;
            Q23=makeQuery(id+"F2.imprint","IMPRINT",FACE,{"disambiguationData":[TD([[makeQuery(id+"F2.imprint","IMPRINT",EDGE,{"derivedFrom":sQuery(id+"F2.wireOp",EDGE,"E26.6.0.0")}),1.0]])]});
            var Q24;
            Q24=makeQuery(id+"F2.imprint","IMPRINT",FACE,{"disambiguationData":[TD([[makeQuery(id+"F2.imprint","IMPRINT",EDGE,{"derivedFrom":sQuery(id+"F2.wireOp",EDGE,"E26.5.0.0")}),1.0]])]});
            var Q25;
            Q25=makeQuery(id+"F2.imprint","IMPRINT",FACE,{"disambiguationData":[TD([[makeQuery(id+"F2.imprint","IMPRINT",EDGE,{"derivedFrom":sQuery(id+"F2.wireOp",EDGE,"E26.4.0.0")}),1.0]])]});
            var Q26;
            Q26=makeQuery(id+"F2.imprint","IMPRINT",FACE,{"disambiguationData":[TD([[makeQuery(id+"F2.imprint","IMPRINT",EDGE,{"derivedFrom":sQuery(id+"F2.wireOp",EDGE,"E26.3.0.0")}),1.0]])]});
            var Q27;
            Q27=makeQuery(id+"F2.imprint","IMPRINT",FACE,{"disambiguationData":[TD([[makeQuery(id+"F2.imprint","IMPRINT",EDGE,{"derivedFrom":sQuery(id+"F2.wireOp",EDGE,"E26.2.0.0")}),1.0]])]});
            var Q28;
            Q28=makeQuery(id+"F2.imprint","IMPRINT",FACE,{"disambiguationData":[TD([[makeQuery(id+"F2.imprint","IMPRINT",EDGE,{"derivedFrom":sQuery(id+"F2.wireOp",EDGE,"E26.1.0.0")}),1.0]])]});
            var Q29;
            Q29=makeQuery(id+"F2.imprint","IMPRINT",FACE,{"disambiguationData":[TD([[makeQuery(id+"F2.imprint","IMPRINT",EDGE,{"derivedFrom":sQuery(id+"F2.wireOp",EDGE,"E20.6.0.0")}),1.0]])]});
            var Q30;
            Q30=makeQuery(id+"F2.imprint","IMPRINT",FACE,{"disambiguationData":[TD([[makeQuery(id+"F2.imprint","IMPRINT",EDGE,{"derivedFrom":sQuery(id+"F2.wireOp",EDGE,"E27.1.0.0")}),1.0]])]});
            var Q31;
            Q31=makeQuery(id+"F2.imprint","IMPRINT",FACE,{"disambiguationData":[TD([[makeQuery(id+"F2.imprint","IMPRINT",EDGE,{"derivedFrom":sQuery(id+"F2.wireOp",EDGE,"E27.2.0.0")}),1.0]])]});
            var Q32;
            Q32=makeQuery(id+"F2.imprint","IMPRINT",FACE,{"disambiguationData":[TD([[makeQuery(id+"F2.imprint","IMPRINT",EDGE,{"derivedFrom":sQuery(id+"F2.wireOp",EDGE,"E27.3.0.0")}),1.0]])]});
            var Q33;
            Q33=makeQuery(id+"F2.imprint","IMPRINT",FACE,{"disambiguationData":[TD([[makeQuery(id+"F2.imprint","IMPRINT",EDGE,{"derivedFrom":sQuery(id+"F2.wireOp",EDGE,"E27.4.0.0")}),1.0]])]});
            var Q34;
            Q34=makeQuery(id+"F2.imprint","IMPRINT",FACE,{"disambiguationData":[TD([[makeQuery(id+"F2.imprint","IMPRINT",EDGE,{"derivedFrom":sQuery(id+"F2.wireOp",EDGE,"E27.5.0.0")}),1.0]])]});
            var Q35;
            Q35=makeQuery(id+"F2.imprint","IMPRINT",FACE,{"disambiguationData":[TD([[makeQuery(id+"F2.imprint","IMPRINT",EDGE,{"derivedFrom":sQuery(id+"F2.wireOp",EDGE,"E27.6.0.0")}),1.0]])]});
            var Q36;
            Q36=makeQuery(id+"F2.imprint","IMPRINT",FACE,{"disambiguationData":[TD([[makeQuery(id+"F2.imprint","IMPRINT",EDGE,{"derivedFrom":sQuery(id+"F2.wireOp",EDGE,"E28.5.0.0")}),1.0]])]});
            var Q37;
            Q37=makeQuery(id+"F2.imprint","IMPRINT",FACE,{"disambiguationData":[TD([[makeQuery(id+"F2.imprint","IMPRINT",EDGE,{"derivedFrom":sQuery(id+"F2.wireOp",EDGE,"E28.4.0.0")}),1.0]])]});
            var Q38;
            Q38=makeQuery(id+"F2.imprint","IMPRINT",FACE,{"disambiguationData":[TD([[makeQuery(id+"F2.imprint","IMPRINT",EDGE,{"derivedFrom":sQuery(id+"F2.wireOp",EDGE,"E28.3.0.0")}),1.0]])]});
            var Q39;
            Q39=makeQuery(id+"F2.imprint","IMPRINT",FACE,{"disambiguationData":[TD([[makeQuery(id+"F2.imprint","IMPRINT",EDGE,{"derivedFrom":sQuery(id+"F2.wireOp",EDGE,"E28.2.0.0")}),1.0]])]});
            var Q40;
            Q40=makeQuery(id+"F2.imprint","IMPRINT",FACE,{"disambiguationData":[TD([[makeQuery(id+"F2.imprint","IMPRINT",EDGE,{"derivedFrom":sQuery(id+"F2.wireOp",EDGE,"E28.1.0.0")}),1.0]])]});
            var Q41;
            Q41=makeQuery(id+"F2.imprint","IMPRINT",FACE,{"disambiguationData":[TD([[makeQuery(id+"F2.imprint","IMPRINT",EDGE,{"derivedFrom":sQuery(id+"F2.wireOp",EDGE,"E20.5.0.0")}),1.0]])]});
            var Q42;
            Q42=makeQuery(id+"F2.imprint","IMPRINT",FACE,{"disambiguationData":[TD([[makeQuery(id+"F2.imprint","IMPRINT",EDGE,{"derivedFrom":sQuery(id+"F2.wireOp",EDGE,"E20.4.0.0")}),1.0]])]});
            var Q43;
            Q43=makeQuery(id+"F2.imprint","IMPRINT",FACE,{"disambiguationData":[TD([[makeQuery(id+"F2.imprint","IMPRINT",EDGE,{"derivedFrom":sQuery(id+"F2.wireOp",EDGE,"E29.1.0.0")}),1.0]])]});
            var Q44;
            Q44=makeQuery(id+"F2.imprint","IMPRINT",FACE,{"disambiguationData":[TD([[makeQuery(id+"F2.imprint","IMPRINT",EDGE,{"derivedFrom":sQuery(id+"F2.wireOp",EDGE,"E29.2.0.0")}),1.0]])]});
            var Q45;
            Q45=makeQuery(id+"F2.imprint","IMPRINT",FACE,{"disambiguationData":[TD([[makeQuery(id+"F2.imprint","IMPRINT",EDGE,{"derivedFrom":sQuery(id+"F2.wireOp",EDGE,"E29.3.0.0")}),1.0]])]});
            var Q46;
            Q46=makeQuery(id+"F2.imprint","IMPRINT",FACE,{"disambiguationData":[TD([[makeQuery(id+"F2.imprint","IMPRINT",EDGE,{"derivedFrom":sQuery(id+"F2.wireOp",EDGE,"E29.4.0.0")}),1.0]])]});
            var Q47;
            Q47=makeQuery(id+"F2.imprint","IMPRINT",FACE,{"disambiguationData":[TD([[makeQuery(id+"F2.imprint","IMPRINT",EDGE,{"derivedFrom":sQuery(id+"F2.wireOp",EDGE,"E30.3.0.0")}),1.0]])]});
            var Q48;
            Q48=makeQuery(id+"F2.imprint","IMPRINT",FACE,{"disambiguationData":[TD([[makeQuery(id+"F2.imprint","IMPRINT",EDGE,{"derivedFrom":sQuery(id+"F2.wireOp",EDGE,"E30.2.0.0")}),1.0]])]});
            var Q49;
            Q49=makeQuery(id+"F2.imprint","IMPRINT",FACE,{"disambiguationData":[TD([[makeQuery(id+"F2.imprint","IMPRINT",EDGE,{"derivedFrom":sQuery(id+"F2.wireOp",EDGE,"E30.1.0.0")}),1.0]])]});
            var Q50;
            Q50=makeQuery(id+"F2.imprint","IMPRINT",FACE,{"disambiguationData":[TD([[makeQuery(id+"F2.imprint","IMPRINT",EDGE,{"derivedFrom":sQuery(id+"F2.wireOp",EDGE,"E20.3.0.0")}),1.0]])]});
            var Q51;
            Q51=makeQuery(id+"F2.imprint","IMPRINT",FACE,{"disambiguationData":[TD([[makeQuery(id+"F2.imprint","IMPRINT",EDGE,{"derivedFrom":sQuery(id+"F2.wireOp",EDGE,"E20.2.0.0")}),1.0]])]});
            var Q52;
            Q52=makeQuery(id+"F2.imprint","IMPRINT",FACE,{"disambiguationData":[TD([[makeQuery(id+"F2.imprint","IMPRINT",EDGE,{"derivedFrom":sQuery(id+"F2.wireOp",EDGE,"E31.1.0.0")}),1.0]])]});
            var Q53;
            Q53=makeQuery(id+"F2.imprint","IMPRINT",FACE,{"disambiguationData":[TD([[makeQuery(id+"F2.imprint","IMPRINT",EDGE,{"derivedFrom":sQuery(id+"F2.wireOp",EDGE,"E31.2.0.0")}),1.0]])]});
            var Q54;
            Q54=makeQuery(id+"F2.imprint","IMPRINT",FACE,{"disambiguationData":[TD([[makeQuery(id+"F2.imprint","IMPRINT",EDGE,{"derivedFrom":sQuery(id+"F2.wireOp",EDGE,"E32.1.0.0")}),1.0]])]});
            var Q55;
            Q55=makeQuery(id+"F2.imprint","IMPRINT",FACE,{"disambiguationData":[TD([[makeQuery(id+"F2.imprint","IMPRINT",EDGE,{"derivedFrom":sQuery(id+"F2.wireOp",EDGE,"E20.1.0.0")}),1.0]])]});
            var Q56;
            Q56=makeQuery(id+"F2.imprint","IMPRINT",FACE,{"disambiguationData":[TD([[makeQuery(id+"F2.imprint","IMPRINT",EDGE,{"derivedFrom":sQuery(id+"F2.wireOp",EDGE,"E16")}),1.0]])]});
            extrude(context, id + "F3", {"entities" : qUnion([Q0, Q1, Q2, Q3, Q4, Q5, Q6, Q7, Q8, Q9, Q10, Q11, Q12, Q13, Q14, Q15, Q16, Q17, Q18, Q19, Q20, Q21, Q22, Q23, Q24, Q25, Q26, Q27, Q28, Q29, Q30, Q31, Q32, Q33, Q34, Q35, Q36, Q37, Q38, Q39, Q40, Q41, Q42, Q43, Q44, Q45, Q46, Q47, Q48, Q49, Q50, Q51, Q52, Q53, Q54, Q55, Q56]), "operationType" : NewBodyOperationType.REMOVE, "oppositeDirection" : true, "depth" : 50 * mm, "offsetDistance" : 25 * mm});
        }
        {
            var Q0;
            Q0=makeQuery(id+"F1.opExtrude","CAP_FACE",FACE,{"disambiguationData":[OSD([sQuery(id+"F0.wireOp",EDGE,"E0.bottom"),sQuery(id+"F0.wireOp",EDGE,"E0.top"),sQuery(id+"F0.wireOp",EDGE,"E0.left"),sQuery(id+"F0.wireOp",EDGE,"E0.right"),sQuery(id+"F0.wireOp",EDGE,"E1.bottom"),sQuery(id+"F0.wireOp",EDGE,"E1.left"),sQuery(id+"F0.wireOp",EDGE,"E2"),sQuery(id+"F0.wireOp",EDGE,"E3"),sQuery(id+"F0.wireOp",EDGE,"E4"),sQuery(id+"F0.wireOp",EDGE,"E5"),sQuery(id+"F0.wireOp",EDGE,"E6.0.1.0"),sQuery(id+"F0.wireOp",EDGE,"E6.0.1.1"),sQuery(id+"F0.wireOp",EDGE,"E6.0.1.2"),sQuery(id+"F0.wireOp",EDGE,"E6.0.1.3"),sQuery(id+"F0.wireOp",EDGE,"E6.0.2.0"),sQuery(id+"F0.wireOp",EDGE,"E6.0.2.1"),sQuery(id+"F0.wireOp",EDGE,"E6.0.2.2"),sQuery(id+"F0.wireOp",EDGE,"E6.0.2.3"),sQuery(id+"F0.wireOp",EDGE,"E6.0.3.0"),sQuery(id+"F0.wireOp",EDGE,"E6.0.3.1"),sQuery(id+"F0.wireOp",EDGE,"E6.0.3.2"),sQuery(id+"F0.wireOp",EDGE,"E6.0.3.3"),sQuery(id+"F0.wireOp",EDGE,"E6.0.4.0"),sQuery(id+"F0.wireOp",EDGE,"E6.0.4.1"),sQuery(id+"F0.wireOp",EDGE,"E6.0.4.2"),sQuery(id+"F0.wireOp",EDGE,"E6.0.4.3"),sQuery(id+"F0.wireOp",EDGE,"E6.0.5.0"),sQuery(id+"F0.wireOp",EDGE,"E6.0.5.1"),sQuery(id+"F0.wireOp",EDGE,"E6.0.5.2"),sQuery(id+"F0.wireOp",EDGE,"E6.0.5.3"),sQuery(id+"F0.wireOp",EDGE,"E6.0.6.0"),sQuery(id+"F0.wireOp",EDGE,"E6.0.6.1"),sQuery(id+"F0.wireOp",EDGE,"E6.0.6.2"),sQuery(id+"F0.wireOp",EDGE,"E6.0.6.3"),sQuery(id+"F0.wireOp",EDGE,"40c6b932-65dc-4c6a-9198-1c7d5abfdf55.left"),sQuery(id+"F0.wireOp",EDGE,"4dc08b29-1ecd-42ad-b35e-29f79ee9a319"),sQuery(id+"F0.wireOp",EDGE,"decfaac6-e95d-441f-ba2d-ea372cedcc19"),sQuery(id+"F0.wireOp",EDGE,"6106fe94-1f46-4984-a826-aca2afe5a6ee"),sQuery(id+"F0.wireOp",EDGE,"8e71a725-0172-4304-8e76-2353e4aaa7c1"),sQuery(id+"F0.wireOp",EDGE,"E7.0.1.0"),sQuery(id+"F0.wireOp",EDGE,"E7.0.1.1"),sQuery(id+"F0.wireOp",EDGE,"E7.0.1.2"),sQuery(id+"F0.wireOp",EDGE,"E7.0.1.3"),sQuery(id+"F0.wireOp",EDGE,"E7.0.2.0"),sQuery(id+"F0.wireOp",EDGE,"E7.0.2.1"),sQuery(id+"F0.wireOp",EDGE,"E7.0.2.2"),sQuery(id+"F0.wireOp",EDGE,"E7.0.2.3"),sQuery(id+"F0.wireOp",EDGE,"E7.0.3.0"),sQuery(id+"F0.wireOp",EDGE,"E7.0.3.1"),sQuery(id+"F0.wireOp",EDGE,"E7.0.3.2"),sQuery(id+"F0.wireOp",EDGE,"E7.0.3.3"),sQuery(id+"F0.wireOp",EDGE,"E7.0.4.0"),sQuery(id+"F0.wireOp",EDGE,"E7.0.4.1"),sQuery(id+"F0.wireOp",EDGE,"E7.0.4.2"),sQuery(id+"F0.wireOp",EDGE,"E7.0.4.3"),sQuery(id+"F0.wireOp",EDGE,"E7.0.5.0"),sQuery(id+"F0.wireOp",EDGE,"E7.0.5.1"),sQuery(id+"F0.wireOp",EDGE,"E7.0.5.2"),sQuery(id+"F0.wireOp",EDGE,"E7.0.5.3"),sQuery(id+"F0.wireOp",EDGE,"E7.0.6.0"),sQuery(id+"F0.wireOp",EDGE,"E7.0.6.1"),sQuery(id+"F0.wireOp",EDGE,"E7.0.6.2"),sQuery(id+"F0.wireOp",EDGE,"E7.0.6.3"),sQuery(id+"F0.wireOp",EDGE,"ZaMQer84-SF47-TDTb-krbA-Ysjm46Tm6KK2")])],"isStart":false});
            var sketch = newSketch(context, id + "F4", { "sketchPlane" : qUnion([Q0])});
            skLineSegment(sketch, "E33.bottom", {"start": v(-11.86, -27) * mm, "end": v(-6.86, -27) * mm});
            skLineSegment(sketch, "E33.top", {"start": v(-11.86, 4.5) * mm, "end": v(-6.86, 4.5) * mm});
            skLineSegment(sketch, "E33.left", {"start": v(-11.86, -27) * mm, "end": v(-11.86, 4.5) * mm});
            skLineSegment(sketch, "E33.right", {"start": v(-6.86, -27) * mm, "end": v(-6.86, 4.5) * mm});
            skLineSegment(sketch, "E34.bottom", {"start": v(3.14, -27) * mm, "end": v(8.14, -27) * mm});
            skLineSegment(sketch, "E34.top", {"start": v(3.14, 4.5) * mm, "end": v(8.14, 4.5) * mm});
            skLineSegment(sketch, "E34.left", {"start": v(3.14, -27) * mm, "end": v(3.14, 4.5) * mm});
            skLineSegment(sketch, "E34.right", {"start": v(8.14, -27) * mm, "end": v(8.14, 4.5) * mm});
            skLineSegment(sketch, "E35.bottom", {"start": v(26.14, -27) * mm, "end": v(21.14, -27) * mm});
            skLineSegment(sketch, "E35.top", {"start": v(26.14, 4.5) * mm, "end": v(21.14, 4.5) * mm});
            skLineSegment(sketch, "E35.left", {"start": v(26.14, -27) * mm, "end": v(26.14, 4.5) * mm});
            skLineSegment(sketch, "E35.right", {"start": v(21.14, -27) * mm, "end": v(21.14, 4.5) * mm});
            skSolve(sketch);
        }
        {
            var Q0;
            {var subQ0=sQuery(id+"F4.wireOp",EDGE,"E33.left");var subQ1=makeQuery(id+"F1.opExtrude","CAP_EDGE",EDGE,{"disambiguationData":[OSD([sQuery(id+"F0.wireOp",EDGE,"ZaMQer84-SF47-TDTb-krbA-Ysjm46Tm6KK2")])],"isStart":false});var subQ2=makeQuery(id+"F4.imprint","INTERSECT",VERTEX,{"derivedFrom":[subQ1,subQ0]});Q0=makeQuery(id+"F4.imprint","IMPRINT",FACE,{"disambiguationData":[TD([[makeQuery(id+"F4.imprint","IMPRINT",EDGE,{"disambiguationData":[TD([[subQ2,-1.0]])],"derivedFrom":subQ0}),-1.0]])]});}
            var Q1;
            {var subQ0=sQuery(id+"F4.wireOp",EDGE,"E34.left");var subQ1=makeQuery(id+"F1.opExtrude","CAP_EDGE",EDGE,{"disambiguationData":[OSD([sQuery(id+"F0.wireOp",EDGE,"ZaMQer84-SF47-TDTb-krbA-Ysjm46Tm6KK2")])],"isStart":false});var subQ2=makeQuery(id+"F4.imprint","INTERSECT",VERTEX,{"derivedFrom":[subQ1,subQ0]});Q1=makeQuery(id+"F4.imprint","IMPRINT",FACE,{"disambiguationData":[TD([[makeQuery(id+"F4.imprint","IMPRINT",EDGE,{"disambiguationData":[TD([[subQ2,-1.0]])],"derivedFrom":subQ0}),-1.0]])]});}
            var Q2;
            {var subQ0=sQuery(id+"F4.wireOp",EDGE,"E35.left");var subQ1=makeQuery(id+"F1.opExtrude","CAP_EDGE",EDGE,{"disambiguationData":[OSD([sQuery(id+"F0.wireOp",EDGE,"ZaMQer84-SF47-TDTb-krbA-Ysjm46Tm6KK2")])],"isStart":false});var subQ2=makeQuery(id+"F4.imprint","INTERSECT",VERTEX,{"derivedFrom":[subQ1,subQ0]});Q2=makeQuery(id+"F4.imprint","IMPRINT",FACE,{"disambiguationData":[TD([[makeQuery(id+"F4.imprint","IMPRINT",EDGE,{"disambiguationData":[TD([[subQ2,-1.0]])],"derivedFrom":subQ0}),1.0]])]});}
            extrude(context, id + "F5", {"entities" : qUnion([Q0, Q1, Q2]), "operationType" : NewBodyOperationType.ADD, "oppositeDirection" : true, "depth" : 3 * mm, "offsetDistance" : 25 * mm});
        }
        {
            var Q0;
            Q0=makeQuery(id+"F1.opExtrude","SWEPT_BODY",BODY,{"disambiguationData":[OSD([sQuery(id+"F0.wireOp",EDGE,"E0.bottom"),sQuery(id+"F0.wireOp",EDGE,"E0.left"),sQuery(id+"F0.wireOp",EDGE,"E0.right"),sQuery(id+"F0.wireOp",EDGE,"E1.bottom"),sQuery(id+"F0.wireOp",EDGE,"E1.left"),sQuery(id+"F0.wireOp",EDGE,"E2"),sQuery(id+"F0.wireOp",EDGE,"E3"),sQuery(id+"F0.wireOp",EDGE,"E4"),sQuery(id+"F0.wireOp",EDGE,"E5"),sQuery(id+"F0.wireOp",EDGE,"E6.0.1.0"),sQuery(id+"F0.wireOp",EDGE,"E6.0.1.1"),sQuery(id+"F0.wireOp",EDGE,"E6.0.1.2"),sQuery(id+"F0.wireOp",EDGE,"E6.0.1.3"),sQuery(id+"F0.wireOp",EDGE,"E6.0.2.0"),sQuery(id+"F0.wireOp",EDGE,"E6.0.2.1"),sQuery(id+"F0.wireOp",EDGE,"E6.0.2.2"),sQuery(id+"F0.wireOp",EDGE,"E6.0.2.3"),sQuery(id+"F0.wireOp",EDGE,"E6.0.3.0"),sQuery(id+"F0.wireOp",EDGE,"E6.0.3.1"),sQuery(id+"F0.wireOp",EDGE,"E6.0.3.2"),sQuery(id+"F0.wireOp",EDGE,"E6.0.3.3"),sQuery(id+"F0.wireOp",EDGE,"E6.0.4.0"),sQuery(id+"F0.wireOp",EDGE,"E6.0.4.1"),sQuery(id+"F0.wireOp",EDGE,"E6.0.4.2"),sQuery(id+"F0.wireOp",EDGE,"E6.0.4.3"),sQuery(id+"F0.wireOp",EDGE,"E7.0.1.2"),sQuery(id+"F0.wireOp",EDGE,"E7.0.2.0"),sQuery(id+"F0.wireOp",EDGE,"E7.0.2.1"),sQuery(id+"F0.wireOp",EDGE,"E7.0.2.2"),sQuery(id+"F0.wireOp",EDGE,"E7.0.2.3"),sQuery(id+"F0.wireOp",EDGE,"E7.0.3.0"),sQuery(id+"F0.wireOp",EDGE,"E7.0.3.1"),sQuery(id+"F0.wireOp",EDGE,"E7.0.3.2"),sQuery(id+"F0.wireOp",EDGE,"E7.0.3.3"),sQuery(id+"F0.wireOp",EDGE,"E7.0.4.0"),sQuery(id+"F0.wireOp",EDGE,"E7.0.4.1"),sQuery(id+"F0.wireOp",EDGE,"E7.0.4.2"),sQuery(id+"F0.wireOp",EDGE,"E7.0.4.3"),sQuery(id+"F0.wireOp",EDGE,"E7.0.5.0"),sQuery(id+"F0.wireOp",EDGE,"E7.0.5.1"),sQuery(id+"F0.wireOp",EDGE,"E7.0.5.2"),sQuery(id+"F0.wireOp",EDGE,"E7.0.5.3"),sQuery(id+"F0.wireOp",EDGE,"E7.0.6.0"),sQuery(id+"F0.wireOp",EDGE,"E7.0.6.1"),sQuery(id+"F0.wireOp",EDGE,"E7.0.6.2"),sQuery(id+"F0.wireOp",EDGE,"E7.0.6.3"),sQuery(id+"F0.wireOp",EDGE,"E8"),sQuery(id+"F0.wireOp",EDGE,"E9")])]});
            var Q1;
            Q1=makeQuery(id+"F1.opExtrude","CAP_EDGE",EDGE,{"disambiguationData":[OSD([sQuery(id+"F0.wireOp",EDGE,"E8")])],"isStart":true});
            transform(context, id + "F6", {"entities" : qUnion([Q0]), "transformType" : TransformType.ROTATION, "transformAxis" : qUnion([Q1]), "angle" : 180 * degree, "makeCopy" : false});
        }
    });
